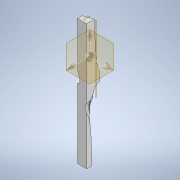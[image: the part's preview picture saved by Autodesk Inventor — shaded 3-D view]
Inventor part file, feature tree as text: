
AUTODESK INVENTOR PART (.ipt)
format: ipt  version: 2022 (Build 260153000, 153)  size: 5,118,464 bytes
history: native  units: mm
features: sketch x8, plane x3, mirror x2, boolean_combine x2, other x2, loft x1, sweep x1, extrude x1, split x1, surface_op x1
ambient origin geometry x8: Origin, YZ Plane, XZ Plane, XY Plane, X Axis, Y Axis, Z Axis, Center Point
bodies: Solid10 (feature_tree), Solid12 (feature_tree), Solid13 (feature_tree)
feature tree (22):
  sketch  "Sketch1"  dims[d3=30.0mm d27=20.0mm]
  sketch  "Sketch2"  dims[d33=7.5mm d34=2.0mm]
  plane  "Work Plane1"
  sketch  "3D Sketch1"
  sketch  "Sketch4"  dims[d35=0.0mm d36=90.0deg d37=0.0mm d38=90.0deg]
  plane  "Work Plane2"
  sketch  "Sketch6"  dims[d39=-7.5mm]
  loft  "Loft1"
  plane  "Work Plane3"
  sweep  "Sweep13"
  mirror  "Mirror3"
  mirror  "Mirror4"
  sketch  "Sketch8"  dims[d43=7.5mm d44=310.0mm d45=0.0mm d46=0.0mm d47=680.0mm d48=90.0deg d49=50.0mm d51=70.0mm d52=0.0mm d53=0.0mm d50=0.5mm d54=0.872665mm]
  boolean_combine  "Combine1"
  extrude  "Extrusion2"  TaperAngle=0.0deg  [1 undecoded]
  boolean_combine  "Combine2"
  split  "Split2"
  sketch  "Sketch7"  dims[d42=20.0mm]
  other  "Pattern of Solid10:2"
  sketch  "3D Sketch2"
  other  "Srf1"
  surface_op  "Boundary Patch1"
note: 1 required parameter value undecoded (feature->parameter linkage not recoverable at this tier; creation-order binding heuristic only, values carry confidence <= 0.55)
